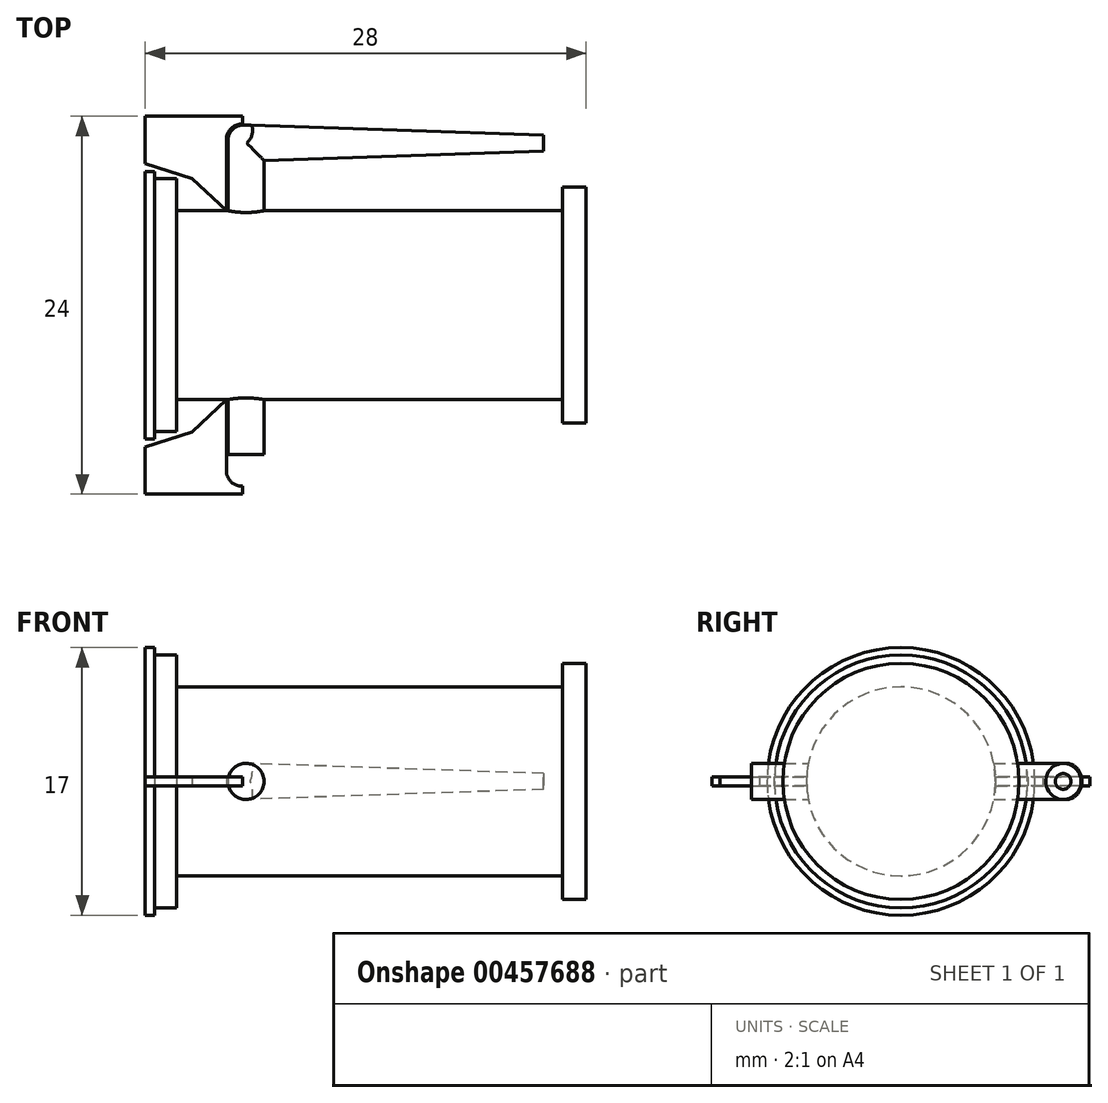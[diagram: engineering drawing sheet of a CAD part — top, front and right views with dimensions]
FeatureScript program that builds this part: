
annotation { "Feature Type Name" : "Feature", "Feature Type Description" : "" }
export const myFeature = defineFeature(function(context is Context, id is Id, definition is map)
    precondition{}
    {
        {
            var Q0;
            Q0=qCreatedBy(makeId("Front.planeOp"),FACE);
            var sketch = newSketch(context, id + "F0", { "sketchPlane" : qUnion([Q0])});
            skLineSegment(sketch, "E0", {"start": v(0, 0) * mm, "end": v(0, 8.5) * mm});
            skLineSegment(sketch, "E1", {"start": v(0, 8.5) * mm, "end": v(0.6, 8.5) * mm});
            skLineSegment(sketch, "E2", {"start": v(0, 0) * mm, "end": v(0, -8.5) * mm});
            skLineSegment(sketch, "E3", {"start": v(0, -8.5) * mm, "end": v(0.55, -8.5) * mm});
            skLineSegment(sketch, "E4", {"start": v(5.18, -5.96) * mm, "end": v(5.18, -10.26) * mm});
            skLineSegment(sketch, "E5", {"start": v(5.18, -10.26) * mm, "end": v(7.58, -10.26) * mm});
            skLineSegment(sketch, "E6", {"start": v(5.2, 5.87) * mm, "end": v(5.2, 11.62) * mm});
            skLineSegment(sketch, "E7", {"start": v(5.2, 11.62) * mm, "end": v(25.3, 10.8) * mm});
            skLineSegment(sketch, "E8", {"start": v(25.3, 10.8) * mm, "end": v(25.3, 9.8) * mm});
            skLineSegment(sketch, "E9", {"start": v(25.3, 9.8) * mm, "end": v(7.58, 9.38) * mm});
            skLineSegment(sketch, "E10", {"start": v(7.58, 9.38) * mm, "end": v(7.58, 5.88) * mm});
            skLineSegment(sketch, "E11", {"start": v(7.58, 5.88) * mm, "end": v(5.2, 5.87) * mm});
            skSolve(sketch);
        }
        {
            var Q0;
            Q0=qCreatedBy(makeId("Front.planeOp"),FACE);
            var sketch = newSketch(context, id + "F1", { "sketchPlane" : qUnion([Q0])});
            skLineSegment(sketch, "E12", {"start": v(0, 0) * mm, "end": v(0, 8.5) * mm});
            skLineSegment(sketch, "E13", {"start": v(0, 8.5) * mm, "end": v(0.6, 8.5) * mm});
            skLineSegment(sketch, "E14", {"start": v(0.6, 8.5) * mm, "end": v(0.6, 8.04) * mm});
            skLineSegment(sketch, "E15", {"start": v(0.6, 8.04) * mm, "end": v(2, 8.04) * mm});
            skLineSegment(sketch, "E16", {"start": v(2, 8.04) * mm, "end": v(2, 6) * mm});
            skLineSegment(sketch, "E17", {"start": v(2, 6) * mm, "end": v(26.5, 6) * mm});
            skLineSegment(sketch, "E18", {"start": v(26.5, 6) * mm, "end": v(26.5, 7.5) * mm});
            skLineSegment(sketch, "E19", {"start": v(26.5, 7.5) * mm, "end": v(28, 7.5) * mm});
            skLineSegment(sketch, "E20", {"start": v(28, 7.5) * mm, "end": v(28, 0) * mm});
            skLineSegment(sketch, "E21", {"start": v(28, 0) * mm, "end": v(0, 0) * mm});
            skSolve(sketch);
        }
        {
            var Q0;
            Q0=qSketchRegion(id+"F1",true);
            var Q1;
            Q1=sQuery(id+"F1.wireOp",EDGE,"E21");
            revolve(context, id + "F2", {"entities" : qUnion([Q0]), "axis" : qUnion([Q1]), "revolveType" : RevolveType.FULL});
        }
        {
            var Q0;
            Q0=qCreatedBy(makeId("Front.planeOp"),FACE);
            var sketch = newSketch(context, id + "F3", { "sketchPlane" : qUnion([Q0])});
            skCircle(sketch, "E22", {"center": v(6.4, 0) * mm, "radius": 1.15 * mm});
            skSolve(sketch);
        }
        {
            var Q0;
            Q0=qSketchRegion(id+"F3",true);
            extrude(context, id + "F4", {"entities" : qUnion([Q0]), "operationType" : NewBodyOperationType.ADD, "depth" : (3.5 + 6) * mm, "hasSecondDirection" : true, "secondDirectionOppositeDirection" : true, "secondDirectionDepth" : (4.3 + 6 + 1.15) * mm});
        }
        {
            var Q0;
            Q0=qCreatedBy(makeId("Right.planeOp"),FACE);
            cPlane(context, id + "F5", {"entities" : qUnion([Q0]), "cplaneType" : CPlaneType.OFFSET, "offset" : 25.3 * mm, "width" : 150 * mm, "height" : 150 * mm});
        }
        {
            var Q0;
            Q0=qCreatedBy(id+"F5.planeOp",FACE);
            var sketch = newSketch(context, id + "F6", { "sketchPlane" : qUnion([Q0])});
            skCircle(sketch, "E23", {"center": v(10.3, 0) * mm, "radius": 0.5 * mm});
            skSolve(sketch);
        }
        {
            var Q0;
            Q0=qCreatedBy(makeId("Right.planeOp"),FACE);
            cPlane(context, id + "F7", {"entities" : qUnion([Q0]), "cplaneType" : CPlaneType.OFFSET, "offset" : 6.4 * mm, "width" : 150 * mm, "height" : 150 * mm});
        }
        {
            var Q0;
            Q0=qCreatedBy(id+"F7.planeOp",FACE);
            var sketch = newSketch(context, id + "F8", { "sketchPlane" : qUnion([Q0])});
            skCircle(sketch, "E24", {"center": v(10.3, 0) * mm, "radius": 1.15 * mm});
            skSolve(sketch);
        }
        {
            var Q1;
            Q1=qSketchRegion(id+"F8",true);
            var Q2;
            Q2=qSketchRegion(id+"F6",true);
            loft(context, id + "F9", {"operationType" : NewBodyOperationType.ADD, "sheetProfilesArray" : [{ "sheetProfileEntities" : qUnion([Q1]) }, { "sheetProfileEntities" : qUnion([Q2]) }]});
        }
        {
            var Q0;
            Q0=makeQuery(id+"F9.boolean.opBoolean","SPLIT",EDGE,{"derivedFrom":makeQuery(id+"F4.opExtrude","CAP_EDGE",EDGE,{"disambiguationData":[OSD([sQuery(id+"F3.wireOp",EDGE,"E22")])],"isStart":true})});
            fillet(context, id + "F10", {"entities" : qUnion([Q0]), "radius" : 1 * mm, "tangentPropagation" : true, "allowEdgeOverflow" : false});
        }
        {
            var Q0;
            Q0=qCreatedBy(makeId("Top.planeOp"),FACE);
            var sketch = newSketch(context, id + "F11", { "sketchPlane" : qUnion([Q0])});
            skLineSegment(sketch, "E25", {"start": v(5.15, 6) * mm, "end": v(5.15, 10.5) * mm});
            skLineSegment(sketch, "E26", {"start": v(0, 11.29) * mm, "end": v(0, 9) * mm});
            skLineSegment(sketch, "E27", {"start": v(0, 9) * mm, "end": v(2.97, 8.05) * mm});
            skLineSegment(sketch, "E28", {"start": v(2.97, 8.05) * mm, "end": v(5.15, 6) * mm});
            skArc(sketch, "E29", {"start": v(6.18, 11.5) * mm, "mid": v(5.45, 11.22) * mm, "end": v(5.15, 10.5) * mm});
            skLineSegment(sketch, "E30", {"start": v(6.18, 11.5) * mm, "end": v(6.18, 12) * mm});
            skLineSegment(sketch, "E31", {"start": v(6.18, 12) * mm, "end": v(0, 12) * mm});
            skLineSegment(sketch, "E32", {"start": v(0, 12) * mm, "end": v(0, 11.29) * mm});
            skSolve(sketch);
        }
        {
            var Q0;
            Q0=qSketchRegion(id+"F11",true);
            extrude(context, id + "F12", {"entities" : qUnion([Q0]), "endBound" : BoundingType.SYMMETRIC, "depth" : .6 * mm});
        }
        {
            var Q0;
            Q0=makeQuery(id+"F12.opExtrude","SWEPT_BODY",BODY,{"disambiguationData":[OSD([sQuery(id+"F11.wireOp",EDGE,"E25"),sQuery(id+"F11.wireOp",EDGE,"E26"),sQuery(id+"F11.wireOp",EDGE,"E27"),sQuery(id+"F11.wireOp",EDGE,"E28"),sQuery(id+"F11.wireOp",EDGE,"E29"),sQuery(id+"F11.wireOp",EDGE,"E30"),sQuery(id+"F11.wireOp",EDGE,"E31"),sQuery(id+"F11.wireOp",EDGE,"E32")])]});
            var Q1;
            Q1=qCreatedBy(makeId("Front.planeOp"),FACE);
            mirror(context, id + "F13", {"entities" : qUnion([Q0]), "mirrorPlane" : qUnion([Q1])});
        }
    });
